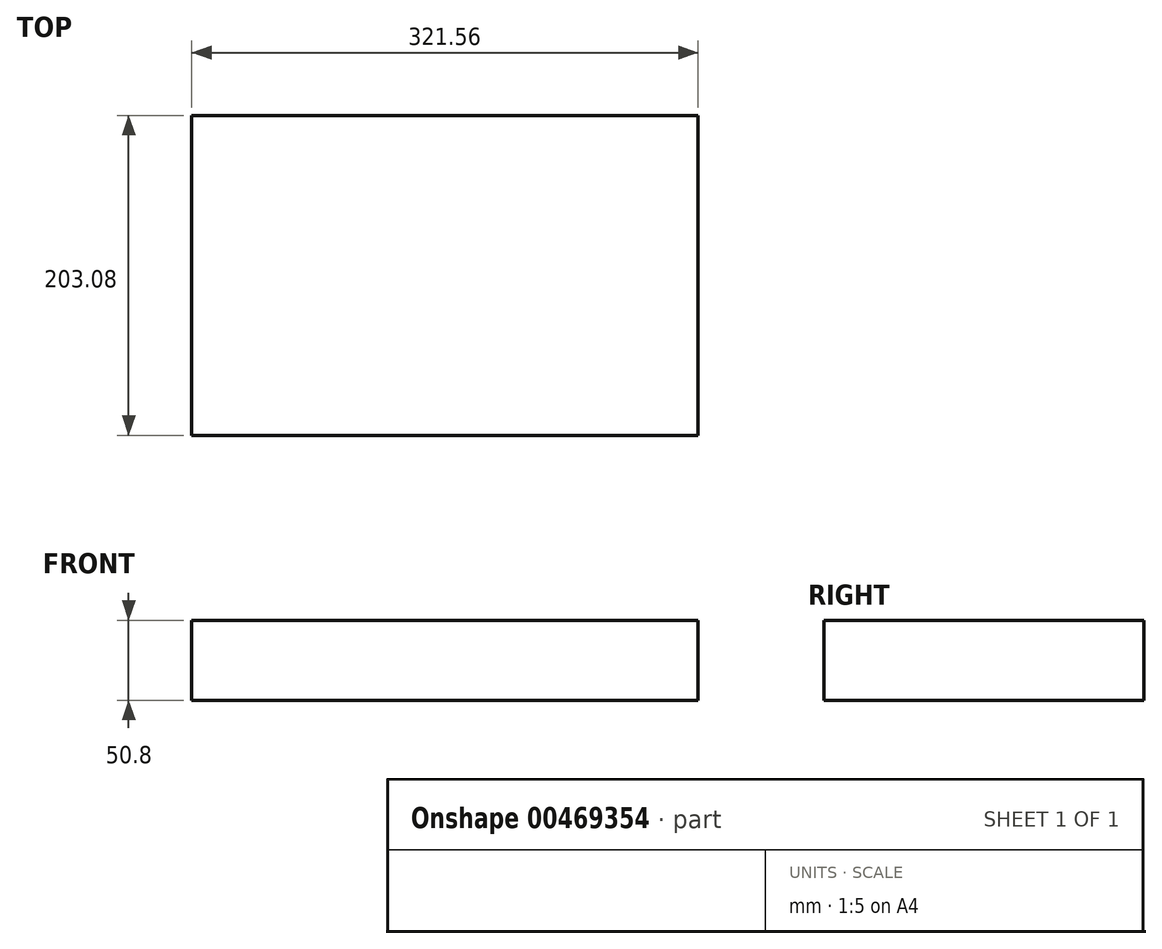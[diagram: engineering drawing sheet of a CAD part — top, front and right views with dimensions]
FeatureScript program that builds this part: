
annotation { "Feature Type Name" : "Feature", "Feature Type Description" : "" }
export const myFeature = defineFeature(function(context is Context, id is Id, definition is map)
    precondition{}
    {
        {
            var Q0;
            Q0=qCreatedBy(makeId("Top.planeOp"),FACE);
            var sketch = newSketch(context, id + "F0", { "sketchPlane" : qUnion([Q0])});
            skLineSegment(sketch, "E0.bottom", {"start": v(160.78, -101.54) * mm, "end": v(-160.78, -101.54) * mm});
            skLineSegment(sketch, "E0.top", {"start": v(160.78, 101.54) * mm, "end": v(-160.78, 101.54) * mm});
            skLineSegment(sketch, "E0.left", {"start": v(160.78, -101.54) * mm, "end": v(160.78, 101.54) * mm});
            skLineSegment(sketch, "E0.right", {"start": v(-160.78, -101.54) * mm, "end": v(-160.78, 101.54) * mm});
            skPoint(sketch, "E0.middle", {"position": v(0, 0) * mm});
            skSolve(sketch);
        }
        {
            var Q0;
            Q0=makeQuery(id+"F0.imprint","IMPRINT",FACE,{"disambiguationData":[TD([[makeQuery(id+"F0.imprint","IMPRINT",EDGE,{"derivedFrom":sQuery(id+"F0.wireOp",EDGE,"E0.bottom")}),-1.0]])]});
            extrude(context, id + "F1", {"entities" : qUnion([Q0]), "depth" : 50.8 * mm});
        }
    });
